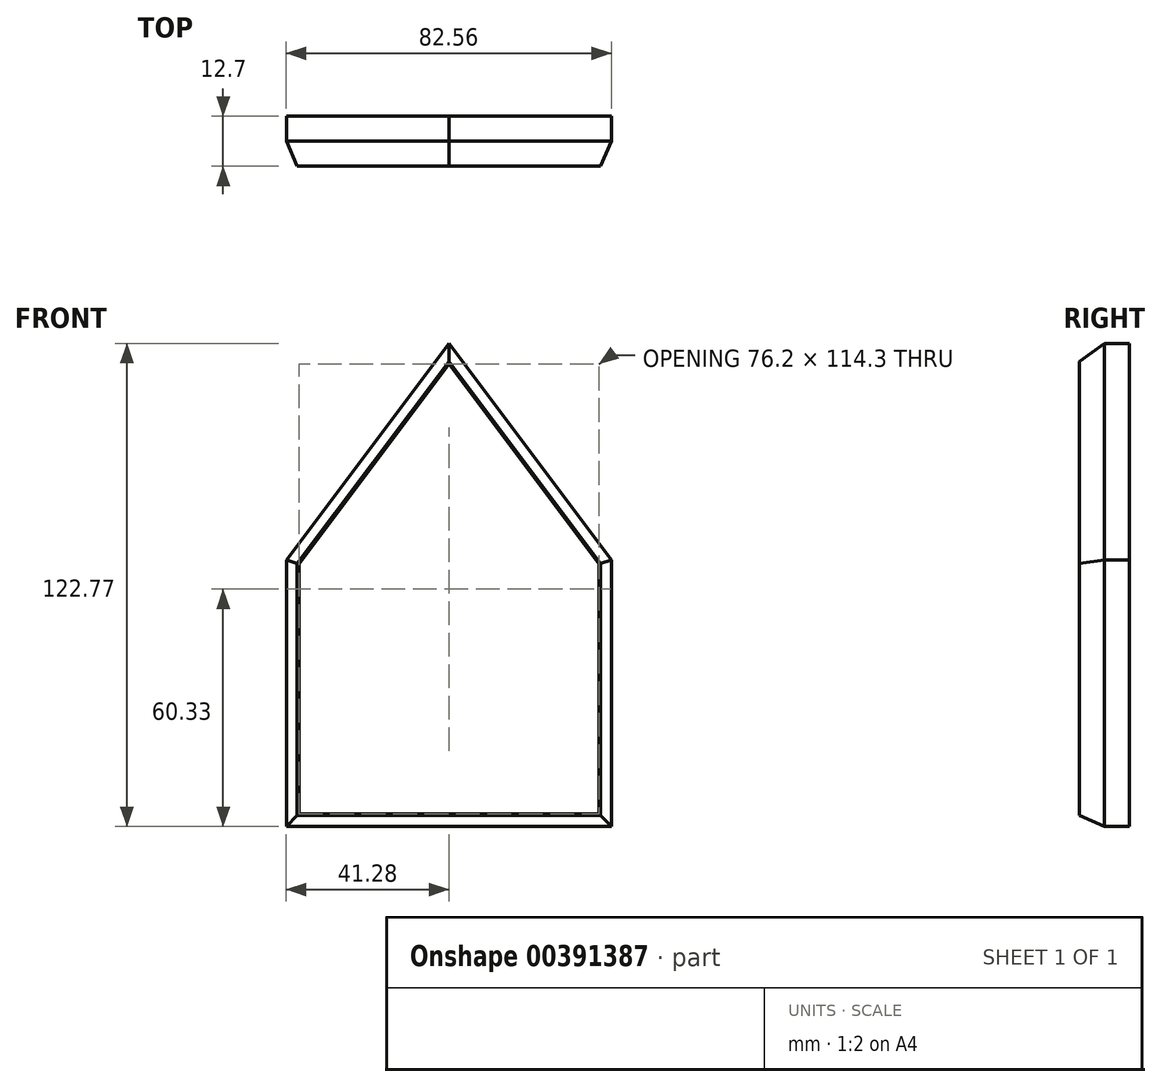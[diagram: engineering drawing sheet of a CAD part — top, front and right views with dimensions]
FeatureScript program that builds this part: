
annotation { "Feature Type Name" : "Feature", "Feature Type Description" : "" }
export const myFeature = defineFeature(function(context is Context, id is Id, definition is map)
    precondition{}
    {
        {
            var Q0;
            Q0=qCreatedBy(makeId("Front.planeOp"),FACE);
            var sketch = newSketch(context, id + "F0", { "sketchPlane" : qUnion([Q0])});
            skLineSegment(sketch, "E0", {"start": v(0, 0) * mm, "end": v(76.2, 0) * mm});
            skLineSegment(sketch, "E1", {"start": v(76.2, 0) * mm, "end": v(76.2, 63.5) * mm});
            skLineSegment(sketch, "E2", {"start": v(38.1, 0) * mm, "end": v(38.1, 114.3) * mm, "construction": true});
            skLineSegment(sketch, "E3", {"start": v(76.2, 63.5) * mm, "end": v(38.1, 114.3) * mm});
            skLineSegment(sketch, "E4", {"start": v(0, 0) * mm, "end": v(0, 63.5) * mm});
            skLineSegment(sketch, "E5", {"start": v(0, 63.5) * mm, "end": v(38.1, 114.3) * mm});
            skLineSegment(sketch, "E6.0", {"start": v(79.38, 64.56) * mm, "end": v(38.1, 119.6) * mm});
            skLineSegment(sketch, "E6.1", {"start": v(-3.18, 64.56) * mm, "end": v(38.1, 119.6) * mm});
            skLineSegment(sketch, "E6.2", {"start": v(79.38, -3.18) * mm, "end": v(79.38, 64.56) * mm});
            skLineSegment(sketch, "E6.3", {"start": v(-3.18, -3.18) * mm, "end": v(79.38, -3.18) * mm});
            skLineSegment(sketch, "E6.4", {"start": v(-3.18, -3.18) * mm, "end": v(-3.18, 64.56) * mm});
            skSolve(sketch);
        }
        {
            var Q0;
            Q0=makeQuery(id+"F0.imprint","IMPRINT",FACE,{"disambiguationData":[TD([[makeQuery(id+"F0.imprint","IMPRINT",EDGE,{"derivedFrom":sQuery(id+"F0.wireOp",EDGE,"E0")}),-1.0]])]});
            extrude(context, id + "F1", {"entities" : qUnion([Q0]), "depth" : 12.7 * mm});
        }
        {
            var Q0;
            Q0=makeQuery(id+"F1.opExtrude","CAP_EDGE",EDGE,{"disambiguationData":[OSD([sQuery(id+"F0.wireOp",EDGE,"E6.3")])],"isStart":false});
            var Q1;
            Q1=makeQuery(id+"F1.opExtrude","CAP_EDGE",EDGE,{"disambiguationData":[OSD([sQuery(id+"F0.wireOp",EDGE,"E6.2")])],"isStart":false});
            var Q2;
            Q2=makeQuery(id+"F1.opExtrude","CAP_EDGE",EDGE,{"disambiguationData":[OSD([sQuery(id+"F0.wireOp",EDGE,"E6.0")])],"isStart":false});
            var Q3;
            Q3=makeQuery(id+"F1.opExtrude","CAP_EDGE",EDGE,{"disambiguationData":[OSD([sQuery(id+"F0.wireOp",EDGE,"E6.1")])],"isStart":false});
            var Q4;
            Q4=makeQuery(id+"F1.opExtrude","CAP_EDGE",EDGE,{"disambiguationData":[OSD([sQuery(id+"F0.wireOp",EDGE,"E6.4")])],"isStart":false});
            chamfer(context, id + "F2", {"entities" : qUnion([Q0, Q1, Q2, Q3, Q4]), "chamferType" : ChamferType.TWO_OFFSETS, "width1" : 2.8 * mm, "oppositeDirection" : false, "width2" : 6.35 * mm, "tangentPropagation" : true});
        }
    });
